# Revit family: BC_Hitachi_Cassette-RCIM-FSR-0.6-2.5_LOD400
name_source: partatom
category: Mechanical Equipment
revit_build: Autodesk Revit 2018 (Build: 20170223_1515(x64)
units: mm (PartAtom-declared; Revit-internal decimal feet)

## family parameters
Cut with Voids When Loaded = No
Host = Face
OmniClass Number = 23.75.70.00
OmniClass Title = HVAC Distribution Devices
Part Type = Normal
Room Calculation Point = No
Round Connector Dimension = Use Diameter
Shared = No

## types (7) — shared parameters
BC_OBJECT_ID = 209115
BC_OBJECT_VERSION = #8
Color = Neutral white (4.56Y8.85/0.38)
Default Elevation = 1219.20 mm
Description = Compact cassette 600 x 600 .Fits perfectly into a false ceiling tile..Individual control setting for each louver.
Face Length = 620.00 mm
Face Width = 620.00 mm
Fan motor input = 57 W
Frequency = 50 Hz
Manufacturer = Hitachi Air Conditioning Europe SAS
MasterFormat = Indoor Central-Station Air-Handling Units
Masterformat Code = 23 73 00
Maximum AC Voltage = 253 V
Minimum AC Voltage = 207 V
Model = Cassette 600 x 600 RCIM FSR
Name BIM&CO = Indoor Unit
Nominal Voltage = 230 V
Number of Poles = 1
OmniClass code = 23-33 25 00
OmniClass description = Air Handling Units
Outlet Diameter = 32.00 mm
Overall depth = 285.00 mm
Overall height = 570.00 mm
Overall width = 570.00 mm
Refrigerant Type = R410A / R32
Uniformat = Distribution Systems
Uniformat code = D3040
Usage Current = 5 A

## per-type parameters (varying)
| type | Acoustic Pressure Level Maxi | Acoustic Pressure Level Mini | Air Flow (HiH/Hi/Me/low) m3/min | BC_VARIANT_ID | Cooling Capacity | Gas Diameter | Heating Capacity | Liquid Diameter | Mass | Maximum Air Flow | Minimum Air Flow | Product Code | Sound power at rated load | Type Comments |
| RCIM-2.5FSRE | 47 | 35 | 16/14/12/10 | 508738 | 6 kW | 15.88 mm | 6 kW | 9.52 mm | 20.00 kg | 16000.0 L/min | 10000.0 L/min | 7E414104 | 60 | RCIM-2.5FSRE |
| RCIM-2.0FSRE | 45 | 31 | 15/12/10/8 | 508742 | 5 kW | 12.70 mm | 6 kW | 6.35 mm | 20.00 kg | 15000.0 L/min | 8000.0 L/min | 7E414103 | 56 | RCIM-2.0FSRE |
| RCIM-1.5FSRE | 41 | 27.5 | 13/11/9.5/7 | 508741 | 4 kW | 12.70 mm | 4 kW | 6.35 mm | 19.00 kg | 13000.0 L/min | 7000.0 L/min | 7E414102 | 54 | RCIM-0.4FSRE |
| RCIM-1.0FSRE | 38 | 24.5 | 12/10/8.5/6 | 508740 | 3 kW | 12.70 mm | 3 kW | 6.35 mm | 19.00 kg | 12000.0 L/min | 6000.0 L/min | 7E414101 | 51 | RCIM-1.0FSRE |
| RCIM-0.8FSRE | 36 | 24.5 | 11/9.5/8/6 | 508744 | 2 kW | 12.70 mm | 2 kW | 6.35 mm | 19.00 kg | 11000.0 L/min | 6000.0 L/min | 7E414100 | 50 | RCIM-0.8FSRE |
| RCIM-0.6FSRE | 34 | 24.5 | 10/8.5/7.5/6 | 508739 | 2 kW | 12.70 mm | 2 kW | 6.35 mm | 19.00 kg | 10000.0 L/min | 6000.0 L/min | 7E414137 | 47 | RCIM-0.6FSRE |
| RCIM-0.4FSRE | 0 | 0 | 10/8.5/7.5/6 | 508743 | 1 kW | 12.70 mm | 1 kW | 6.35 mm | 18.50 kg | 8500.0 L/min | 6000.0 L/min | 7E414148 | 43 | RCIM-0.4FSRE |

note: column(s) folded — value = type name in every type: Reference
